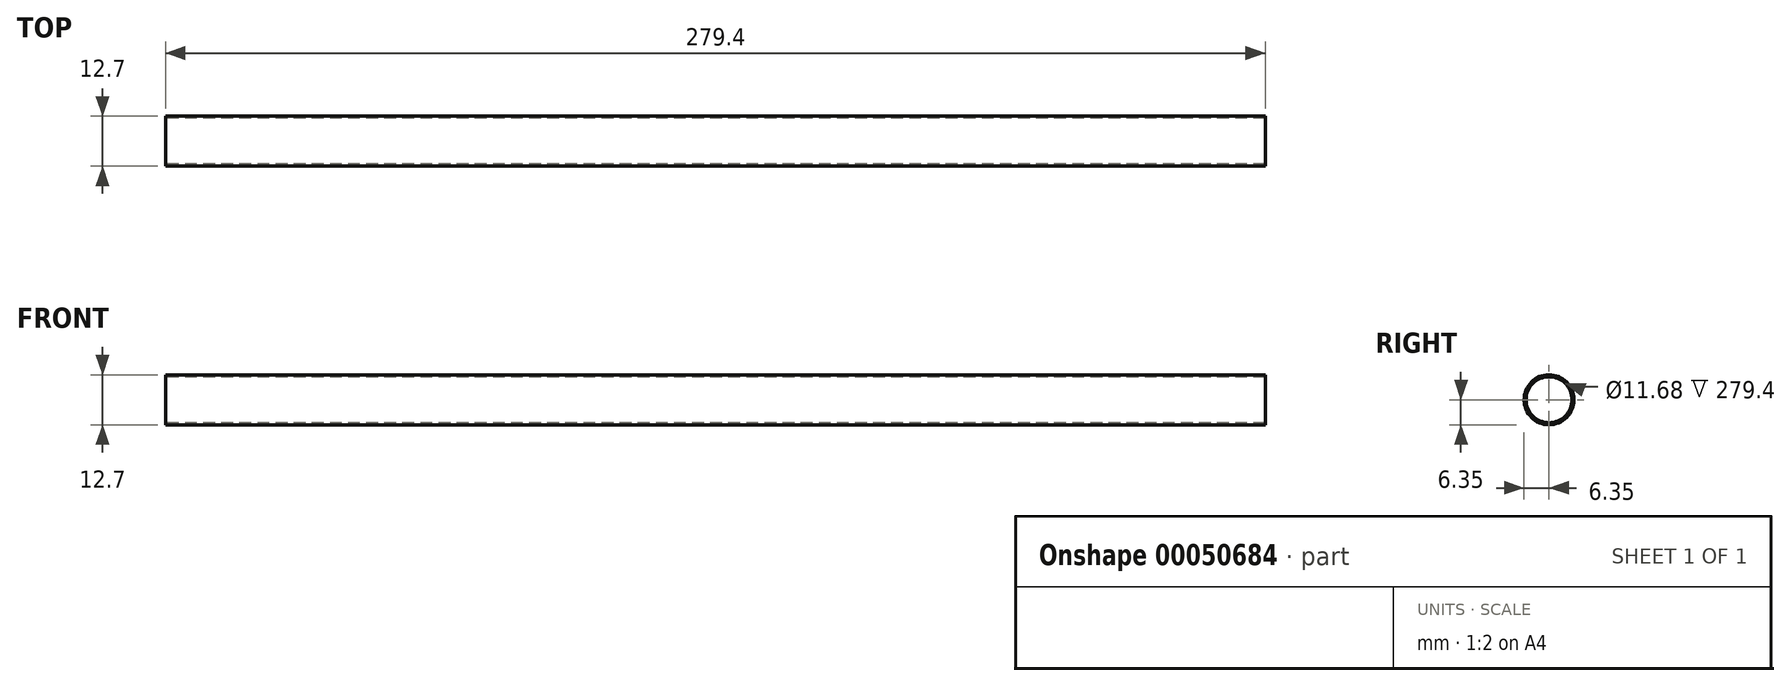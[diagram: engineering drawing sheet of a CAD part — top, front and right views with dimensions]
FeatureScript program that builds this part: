
annotation { "Feature Type Name" : "Feature", "Feature Type Description" : "" }
export const myFeature = defineFeature(function(context is Context, id is Id, definition is map)
    precondition{}
    {
        {
            var Q0;
            Q0=qCreatedBy(makeId("Right.planeOp"),FACE);
            var sketch = newSketch(context, id + "F0", { "sketchPlane" : qUnion([Q0])});
            skCircle(sketch, "E0", {"center": v(0, 0) * mm, "radius": 6.35 * mm});
            skSolve(sketch);
        }
        {
            var Q0;
            Q0 = qSketchRegion(id + "F0", true);
            extrude(context, id + "F1", {"entities" : qUnion([Q0]), "depth" : 279.4 * mm});
        }
        {
            var Q0;
            Q0=qCreatedBy(makeId("Right.planeOp"),FACE);
            var sketch = newSketch(context, id + "F2", { "sketchPlane" : qUnion([Q0])});
            skCircle(sketch, "E1", {"center": v(0, 0) * mm, "radius": 5.84 * mm});
            skSolve(sketch);
        }
        {
            var Q0;
            Q0=makeQuery(id+"F2.imprint","IMPRINT",FACE,{"disambiguationData":[TD([[makeQuery(id+"F2.imprint","IMPRINT",EDGE,{"derivedFrom":sQuery(id+"F2.wireOp",EDGE,"E1")}),1.0]])]});
            extrude(context, id + "F3", {"entities" : qUnion([Q0]), "operationType" : NewBodyOperationType.REMOVE, "endBound" : BoundingType.UP_TO_NEXT, "depth" : 25.4 * mm});
        }
    });
